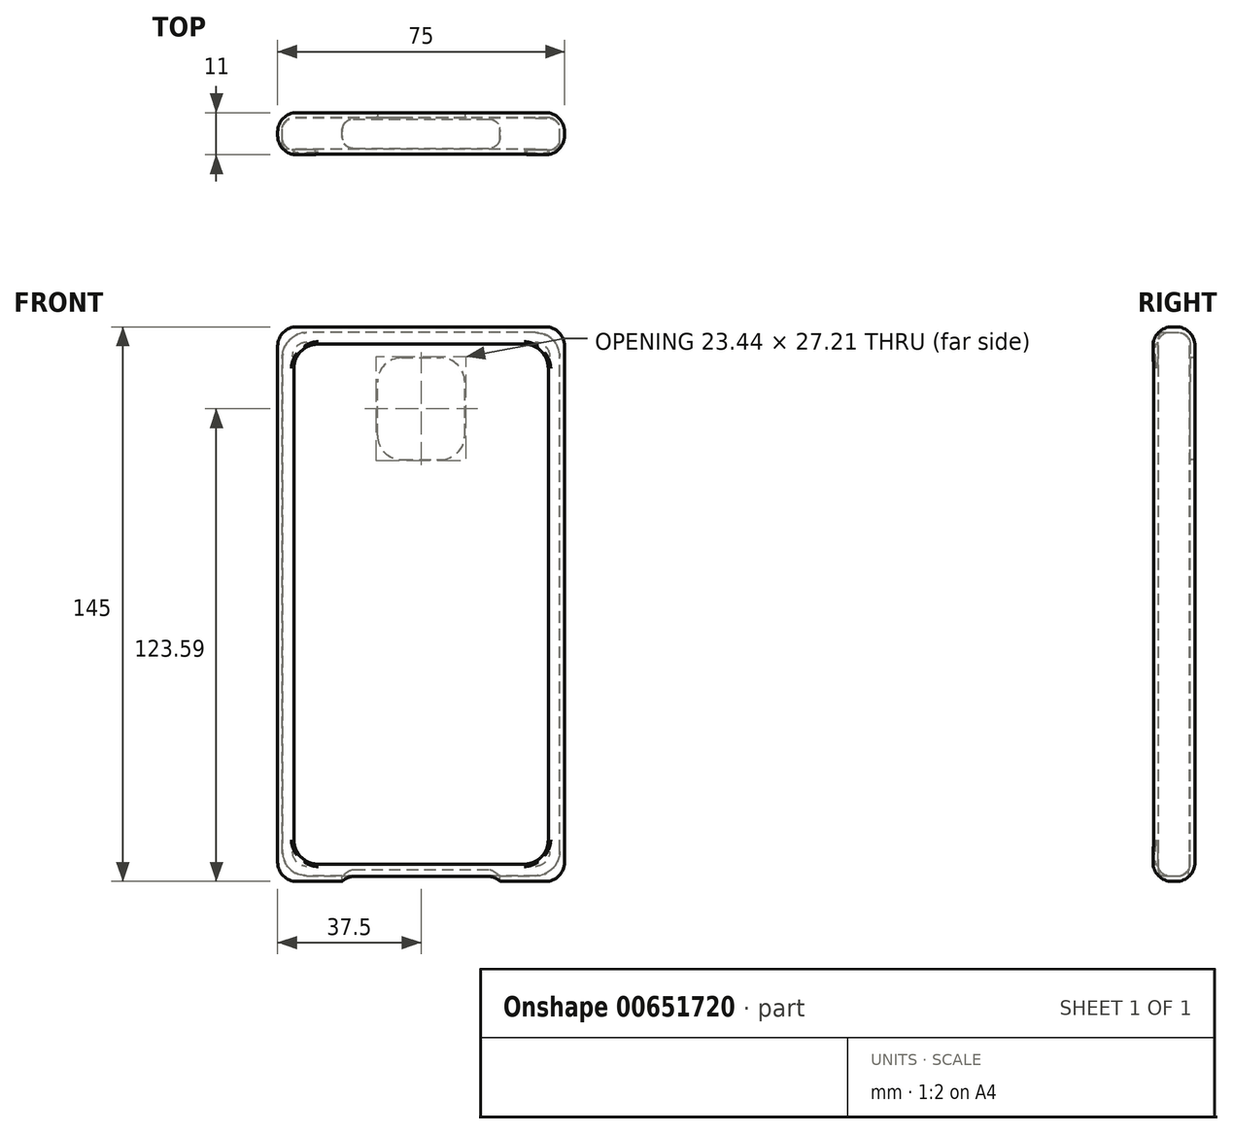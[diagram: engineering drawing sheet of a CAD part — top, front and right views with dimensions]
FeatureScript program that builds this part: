
annotation { "Feature Type Name" : "Feature", "Feature Type Description" : "" }
export const myFeature = defineFeature(function(context is Context, id is Id, definition is map)
    precondition{}
    {
        {
            var Q0;
            Q0=qCreatedBy(makeId("Front.planeOp"),FACE);
            var sketch = newSketch(context, id + "F0", { "sketchPlane" : qUnion([Q0])});
            skLineSegment(sketch, "E0.bottom", {"start": v(29.9, -71) * mm, "end": v(-29.9, -71) * mm});
            skLineSegment(sketch, "E0.top", {"start": v(29.9, 71) * mm, "end": v(-29.9, 71) * mm});
            skLineSegment(sketch, "E0.left", {"start": v(36.25, -64.65) * mm, "end": v(36.25, 64.65) * mm});
            skLineSegment(sketch, "E0.right", {"start": v(-36.25, -64.65) * mm, "end": v(-36.25, 64.65) * mm});
            skPoint(sketch, "E0.middle", {"position": v(0, 0) * mm});
            skPoint(sketch, "E1.visualSharp", {"position": v(-36.25, 71) * mm});
            skArc(sketch, "E1.filletArc", {"start": v(-29.9, 71) * mm, "mid": v(-34.4, 69.14) * mm, "end": v(-36.25, 64.65) * mm});
            skPoint(sketch, "E2.visualSharp", {"position": v(36.25, 71) * mm});
            skArc(sketch, "E2.filletArc", {"start": v(36.25, 64.65) * mm, "mid": v(34.4, 69.14) * mm, "end": v(29.9, 71) * mm});
            skPoint(sketch, "E3.visualSharp", {"position": v(36.25, -71) * mm});
            skArc(sketch, "E3.filletArc", {"start": v(29.9, -71) * mm, "mid": v(34.4, -69.14) * mm, "end": v(36.25, -64.65) * mm});
            skPoint(sketch, "E4.visualSharp", {"position": v(-36.25, -71) * mm});
            skArc(sketch, "E4.filletArc", {"start": v(-36.25, -64.65) * mm, "mid": v(-34.4, -69.14) * mm, "end": v(-29.9, -71) * mm});
            skSolve(sketch);
        }
        {
            var Q0;
            Q0=makeQuery(id+"F0.imprint","IMPRINT",FACE,{"disambiguationData":[TD([[makeQuery(id+"F0.imprint","IMPRINT",EDGE,{"derivedFrom":sQuery(id+"F0.wireOp",EDGE,"E0.bottom")}),-1.0]])]});
            extrude(context, id + "F1", {"entities" : qUnion([Q0]), "endBound" : BoundingType.SYMMETRIC, "depth" : 8.1 * mm, "offsetDistance" : 25.4 * mm});
        }
        {
            var Q0;
            Q0=makeQuery(id+"F1.opExtrude","CAP_FACE",FACE,{"disambiguationData":[OSD([sQuery(id+"F0.wireOp",EDGE,"E0.bottom"),sQuery(id+"F0.wireOp",EDGE,"E0.top"),sQuery(id+"F0.wireOp",EDGE,"E0.left"),sQuery(id+"F0.wireOp",EDGE,"E0.right"),sQuery(id+"F0.wireOp",EDGE,"E1.filletArc"),sQuery(id+"F0.wireOp",EDGE,"E2.filletArc"),sQuery(id+"F0.wireOp",EDGE,"E3.filletArc"),sQuery(id+"F0.wireOp",EDGE,"E4.filletArc")])],"isStart":false});
            fillet(context, id + "F2", {"entities" : qUnion([Q0]), "radius" : 1.27 * mm, "tangentPropagation" : true, "allowEdgeOverflow" : false});
        }
        {
            var Q0;
            Q0=makeQuery(id+"F1.opExtrude","CAP_FACE",FACE,{"disambiguationData":[OSD([sQuery(id+"F0.wireOp",EDGE,"E0.bottom"),sQuery(id+"F0.wireOp",EDGE,"E0.top"),sQuery(id+"F0.wireOp",EDGE,"E0.left"),sQuery(id+"F0.wireOp",EDGE,"E0.right"),sQuery(id+"F0.wireOp",EDGE,"E1.filletArc"),sQuery(id+"F0.wireOp",EDGE,"E2.filletArc"),sQuery(id+"F0.wireOp",EDGE,"E3.filletArc"),sQuery(id+"F0.wireOp",EDGE,"E4.filletArc")])],"isStart":true});
            fillet(context, id + "F3", {"entities" : qUnion([Q0]), "radius" : 2.54 * mm, "rho" : .3, "crossSection" : FilletCrossSection.CONIC, "allowEdgeOverflow" : false});
        }
        {
            var Q0;
            Q0=qCreatedBy(makeId("Front.planeOp"),FACE);
            var sketch = newSketch(context, id + "F4", { "sketchPlane" : qUnion([Q0])});
            skLineSegment(sketch, "E5.bottom", {"start": v(37.5, -72.5) * mm, "end": v(-37.5, -72.5) * mm});
            skLineSegment(sketch, "E5.top", {"start": v(37.5, 72.5) * mm, "end": v(-37.5, 72.5) * mm});
            skLineSegment(sketch, "E5.left", {"start": v(37.5, -72.5) * mm, "end": v(37.5, 72.5) * mm});
            skLineSegment(sketch, "E5.right", {"start": v(-37.5, -72.5) * mm, "end": v(-37.5, 72.5) * mm});
            skPoint(sketch, "E5.middle", {"position": v(0, 0) * mm});
            skSolve(sketch);
        }
        {
            var Q0;
            Q0 = qSketchRegion(id + "F4", true);
            extrude(context, id + "F5", {"entities" : qUnion([Q0]), "endBound" : BoundingType.SYMMETRIC, "depth" : 11 * mm, "offsetDistance" : 25 * mm});
        }
        {
            var Q0;
            Q0=makeQuery(id+"F5.opExtrude","SWEPT_EDGE",EDGE,{"disambiguationData":[OSD([sQuery(id+"F4.wireOp",EDGE,"E5.top"),sQuery(id+"F4.wireOp",EDGE,"E5.right")])]});
            var Q1;
            Q1=makeQuery(id+"F5.opExtrude","SWEPT_EDGE",EDGE,{"disambiguationData":[OSD([sQuery(id+"F4.wireOp",EDGE,"E5.top"),sQuery(id+"F4.wireOp",EDGE,"E5.left")])]});
            var Q2;
            Q2=makeQuery(id+"F5.opExtrude","SWEPT_EDGE",EDGE,{"disambiguationData":[OSD([sQuery(id+"F4.wireOp",EDGE,"E5.bottom"),sQuery(id+"F4.wireOp",EDGE,"E5.right")])]});
            var Q3;
            Q3=makeQuery(id+"F5.opExtrude","SWEPT_EDGE",EDGE,{"disambiguationData":[OSD([sQuery(id+"F4.wireOp",EDGE,"E5.bottom"),sQuery(id+"F4.wireOp",EDGE,"E5.left")])]});
            fillet(context, id + "F6", {"entities" : qUnion([Q0, Q1, Q2, Q3]), "radius" : 5 * mm, "tangentPropagation" : true, "allowEdgeOverflow" : false});
        }
        {
            var Q0;
            Q0=makeQuery(id+"F5.opExtrude","CAP_FACE",FACE,{"disambiguationData":[OSD([sQuery(id+"F4.wireOp",EDGE,"E5.bottom"),sQuery(id+"F4.wireOp",EDGE,"E5.top"),sQuery(id+"F4.wireOp",EDGE,"E5.left"),sQuery(id+"F4.wireOp",EDGE,"E5.right")])],"isStart":false});
            var Q1;
            Q1=makeQuery(id+"F5.opExtrude","CAP_FACE",FACE,{"disambiguationData":[OSD([sQuery(id+"F4.wireOp",EDGE,"E5.bottom"),sQuery(id+"F4.wireOp",EDGE,"E5.top"),sQuery(id+"F4.wireOp",EDGE,"E5.left"),sQuery(id+"F4.wireOp",EDGE,"E5.right")])],"isStart":true});
            fillet(context, id + "F7", {"entities" : qUnion([Q0, Q1]), "radius" : 5 * mm, "tangentPropagation" : true, "allowEdgeOverflow" : false});
        }
        {
            var Q0;
            Q0=qCreatedBy(makeId("Front.planeOp"),FACE);
            var sketch = newSketch(context, id + "F8", { "sketchPlane" : qUnion([Q0])});
            skLineSegment(sketch, "E6.bottom", {"start": v(30.1, -71.2) * mm, "end": v(-30.1, -71.2) * mm});
            skLineSegment(sketch, "E6.top", {"start": v(30.1, 71.2) * mm, "end": v(-30.1, 71.2) * mm});
            skLineSegment(sketch, "E6.left", {"start": v(36.45, -64.85) * mm, "end": v(36.45, 64.85) * mm});
            skLineSegment(sketch, "E6.right", {"start": v(-36.45, -64.85) * mm, "end": v(-36.45, 64.85) * mm});
            skPoint(sketch, "E6.middle", {"position": v(0, 0) * mm});
            skPoint(sketch, "E7.visualSharp", {"position": v(-36.45, 71.2) * mm});
            skArc(sketch, "E7.filletArc", {"start": v(-30.1, 71.2) * mm, "mid": v(-34.6, 69.34) * mm, "end": v(-36.45, 64.85) * mm});
            skPoint(sketch, "E8.visualSharp", {"position": v(36.45, 71.2) * mm});
            skArc(sketch, "E8.filletArc", {"start": v(36.45, 64.85) * mm, "mid": v(34.6, 69.34) * mm, "end": v(30.1, 71.2) * mm});
            skPoint(sketch, "E9.visualSharp", {"position": v(36.45, -71.2) * mm});
            skArc(sketch, "E9.filletArc", {"start": v(30.1, -71.2) * mm, "mid": v(34.6, -69.34) * mm, "end": v(36.45, -64.85) * mm});
            skPoint(sketch, "E10.visualSharp", {"position": v(-36.45, -71.2) * mm});
            skArc(sketch, "E10.filletArc", {"start": v(-36.45, -64.85) * mm, "mid": v(-34.6, -69.34) * mm, "end": v(-30.1, -71.2) * mm});
            skLineSegment(sketch, "E11.bottom", {"start": v(26.9, -68) * mm, "end": v(-26.9, -68) * mm});
            skLineSegment(sketch, "E11.top", {"start": v(26.9, 68) * mm, "end": v(-26.9, 68) * mm});
            skLineSegment(sketch, "E11.left", {"start": v(33.25, -61.65) * mm, "end": v(33.25, 61.65) * mm});
            skLineSegment(sketch, "E11.right", {"start": v(-33.25, -61.65) * mm, "end": v(-33.25, 61.65) * mm});
            skPoint(sketch, "E12.visualSharp", {"position": v(-33.25, 68) * mm});
            skArc(sketch, "E12.filletArc", {"start": v(-26.9, 68) * mm, "mid": v(-31.4, 66.14) * mm, "end": v(-33.25, 61.65) * mm});
            skPoint(sketch, "E13.visualSharp", {"position": v(33.25, 68) * mm});
            skArc(sketch, "E13.filletArc", {"start": v(33.25, 61.65) * mm, "mid": v(31.4, 66.14) * mm, "end": v(26.9, 68) * mm});
            skPoint(sketch, "E14.visualSharp", {"position": v(-33.25, -68) * mm});
            skArc(sketch, "E14.filletArc", {"start": v(-33.25, -61.65) * mm, "mid": v(-31.4, -66.14) * mm, "end": v(-26.9, -68) * mm});
            skPoint(sketch, "E15.visualSharp", {"position": v(33.25, -68) * mm});
            skArc(sketch, "E15.filletArc", {"start": v(26.9, -68) * mm, "mid": v(31.4, -66.14) * mm, "end": v(33.25, -61.65) * mm});
            skSolve(sketch);
        }
        {
            var Q0;
            Q0=makeQuery(id+"F0.imprint","IMPRINT",FACE,{"disambiguationData":[TD([[makeQuery(id+"F0.imprint","IMPRINT",EDGE,{"derivedFrom":sQuery(id+"F0.wireOp",EDGE,"E0.bottom")}),-1.0]])]});
            var Q1;
            Q1=makeQuery(id+"F8.imprint","IMPRINT",FACE,{"disambiguationData":[TD([[makeQuery(id+"F8.imprint","IMPRINT",EDGE,{"derivedFrom":sQuery(id+"F8.wireOp",EDGE,"E11.bottom")}),-1.0]])]});
            extrude(context, id + "F9", {"entities" : qUnion([Q0, Q1]), "endBound" : BoundingType.SYMMETRIC, "depth" : 8.5 * mm, "offsetDistance" : 25 * mm});
        }
        {
            var Q0;
            Q0=makeQuery(id+"F9.opExtrude","SWEPT_BODY",BODY,{"disambiguationData":[OSD([sQuery(id+"F8.wireOp",EDGE,"E11.bottom"),sQuery(id+"F8.wireOp",EDGE,"E11.top"),sQuery(id+"F8.wireOp",EDGE,"E11.left"),sQuery(id+"F8.wireOp",EDGE,"E11.right"),sQuery(id+"F8.wireOp",EDGE,"E12.filletArc"),sQuery(id+"F8.wireOp",EDGE,"E13.filletArc"),sQuery(id+"F8.wireOp",EDGE,"E14.filletArc"),sQuery(id+"F8.wireOp",EDGE,"E15.filletArc")])]});
            transform(context, id + "F10", {"entities" : qUnion([Q0]), "transformType" : TransformType.TRANSLATION_3D, "dx" : 0 * mm, "dy" : -8.5 * mm, "dz" : 0 * mm, "makeCopy" : false});
        }
        {
            var Q0;
            Q0=makeQuery(id+"F9.opExtrude","SWEPT_FACE",FACE,{"disambiguationData":[OSD([sQuery(id+"F0.wireOp",EDGE,"E0.right")])]});
            var Q1;
            Q1=makeQuery(id+"F9.opExtrude","SWEPT_FACE",FACE,{"disambiguationData":[OSD([sQuery(id+"F0.wireOp",EDGE,"E0.bottom")])]});
            var Q2;
            Q2=makeQuery(id+"F9.opExtrude","SWEPT_FACE",FACE,{"disambiguationData":[OSD([sQuery(id+"F0.wireOp",EDGE,"E0.left")])]});
            var Q3;
            Q3=makeQuery(id+"F9.opExtrude","SWEPT_FACE",FACE,{"disambiguationData":[OSD([sQuery(id+"F0.wireOp",EDGE,"E0.top")])]});
            fillet(context, id + "F11", {"entities" : qUnion([Q0, Q1, Q2, Q3]), "radius" : 2.54 * mm, "rho" : .3, "crossSection" : FilletCrossSection.CONIC, "allowEdgeOverflow" : false});
        }
        {
            var Q0;
            Q0=makeQuery(id+"F5.opExtrude","CAP_FACE",FACE,{"disambiguationData":[OSD([sQuery(id+"F4.wireOp",EDGE,"E5.bottom"),sQuery(id+"F4.wireOp",EDGE,"E5.top"),sQuery(id+"F4.wireOp",EDGE,"E5.left"),sQuery(id+"F4.wireOp",EDGE,"E5.right")])],"isStart":true});
            var sketch = newSketch(context, id + "F12", { "sketchPlane" : qUnion([Q0])});
            skLineSegment(sketch, "E16.bottom", {"start": v(5.07, 37.79) * mm, "end": v(-5.07, 37.79) * mm});
            skLineSegment(sketch, "E16.top", {"start": v(5.07, 64.4) * mm, "end": v(-5.07, 64.4) * mm});
            skLineSegment(sketch, "E16.left", {"start": v(11.42, 44.14) * mm, "end": v(11.42, 58.04) * mm});
            skLineSegment(sketch, "E16.right", {"start": v(-11.42, 44.14) * mm, "end": v(-11.42, 58.04) * mm});
            skPoint(sketch, "E16.middle", {"position": v(0, 51.09) * mm});
            skPoint(sketch, "E17.visualSharp", {"position": v(-11.42, 64.4) * mm});
            skArc(sketch, "E17.filletArc", {"start": v(-5.07, 64.4) * mm, "mid": v(-9.56, 62.53) * mm, "end": v(-11.42, 58.04) * mm});
            skPoint(sketch, "E18.visualSharp", {"position": v(11.42, 64.4) * mm});
            skArc(sketch, "E18.filletArc", {"start": v(11.42, 58.04) * mm, "mid": v(9.56, 62.53) * mm, "end": v(5.07, 64.4) * mm});
            skPoint(sketch, "E19.visualSharp", {"position": v(11.42, 37.79) * mm});
            skArc(sketch, "E19.filletArc", {"start": v(5.07, 37.79) * mm, "mid": v(9.56, 39.65) * mm, "end": v(11.42, 44.14) * mm});
            skPoint(sketch, "E20.visualSharp", {"position": v(-11.42, 37.79) * mm});
            skArc(sketch, "E20.filletArc", {"start": v(-11.42, 44.14) * mm, "mid": v(-9.56, 39.65) * mm, "end": v(-5.07, 37.79) * mm});
            skSolve(sketch);
        }
        {
            var Q0;
            Q0=makeQuery(id+"F12.imprint","IMPRINT",FACE,{"disambiguationData":[TD([[makeQuery(id+"F12.imprint","IMPRINT",EDGE,{"derivedFrom":sQuery(id+"F12.wireOp",EDGE,"E16.bottom")}),-1.0]])]});
            extrude(context, id + "F13", {"entities" : qUnion([Q0]), "depth" : 5 * mm, "offsetDistance" : 25 * mm});
        }
        {
            var Q0;
            Q0=makeQuery(id+"F13.opExtrude","SWEPT_BODY",BODY,{"disambiguationData":[OSD([sQuery(id+"F12.wireOp",EDGE,"E16.bottom"),sQuery(id+"F12.wireOp",EDGE,"E16.top"),sQuery(id+"F12.wireOp",EDGE,"E16.left"),sQuery(id+"F12.wireOp",EDGE,"E16.right"),sQuery(id+"F12.wireOp",EDGE,"E17.filletArc"),sQuery(id+"F12.wireOp",EDGE,"E18.filletArc"),sQuery(id+"F12.wireOp",EDGE,"E19.filletArc"),sQuery(id+"F12.wireOp",EDGE,"E20.filletArc")])]});
            transform(context, id + "F14", {"entities" : qUnion([Q0]), "transformType" : TransformType.TRANSLATION_3D, "dx" : 0 * mm, "dy" : -1.5 * mm, "dz" : 0 * mm, "makeCopy" : false});
        }
        {
            var Q0;
            Q0=makeQuery(id+"F9.opExtrude","SWEPT_BODY",BODY,{"disambiguationData":[OSD([sQuery(id+"F0.wireOp",EDGE,"E0.bottom"),sQuery(id+"F0.wireOp",EDGE,"E0.top"),sQuery(id+"F0.wireOp",EDGE,"E0.left"),sQuery(id+"F0.wireOp",EDGE,"E0.right"),sQuery(id+"F0.wireOp",EDGE,"E1.filletArc"),sQuery(id+"F0.wireOp",EDGE,"E2.filletArc"),sQuery(id+"F0.wireOp",EDGE,"E3.filletArc"),sQuery(id+"F0.wireOp",EDGE,"E4.filletArc")])]});
            var Q1;
            Q1=makeQuery(id+"F9.opExtrude","SWEPT_BODY",BODY,{"disambiguationData":[OSD([sQuery(id+"F8.wireOp",EDGE,"E11.bottom"),sQuery(id+"F8.wireOp",EDGE,"E11.top"),sQuery(id+"F8.wireOp",EDGE,"E11.left"),sQuery(id+"F8.wireOp",EDGE,"E11.right"),sQuery(id+"F8.wireOp",EDGE,"E12.filletArc"),sQuery(id+"F8.wireOp",EDGE,"E13.filletArc"),sQuery(id+"F8.wireOp",EDGE,"E14.filletArc"),sQuery(id+"F8.wireOp",EDGE,"E15.filletArc")])]});
            var Q2;
            Q2=makeQuery(id+"F13.opExtrude","SWEPT_BODY",BODY,{"disambiguationData":[OSD([sQuery(id+"F12.wireOp",EDGE,"E16.bottom"),sQuery(id+"F12.wireOp",EDGE,"E16.top"),sQuery(id+"F12.wireOp",EDGE,"E16.left"),sQuery(id+"F12.wireOp",EDGE,"E16.right"),sQuery(id+"F12.wireOp",EDGE,"E17.filletArc"),sQuery(id+"F12.wireOp",EDGE,"E18.filletArc"),sQuery(id+"F12.wireOp",EDGE,"E19.filletArc"),sQuery(id+"F12.wireOp",EDGE,"E20.filletArc")])]});
            var Q3;
            Q3=makeQuery(id+"F5.opExtrude","SWEPT_BODY",BODY,{"disambiguationData":[OSD([sQuery(id+"F4.wireOp",EDGE,"E5.bottom"),sQuery(id+"F4.wireOp",EDGE,"E5.top"),sQuery(id+"F4.wireOp",EDGE,"E5.left"),sQuery(id+"F4.wireOp",EDGE,"E5.right")])]});
            booleanBodies(context, id + "F15", {"operationType" : BooleanOperationType.SUBTRACTION, "tools" : qUnion([Q0, Q1, Q2]), "targets" : qUnion([Q3])});
        }
        {
            var Q0;
            Q0=makeQuery(id+"F15.opBoolean","COPY",FACE,{"derivedFrom":makeQuery(id+"F9.opExtrude","SWEPT_FACE",FACE,{"disambiguationData":[OSD([sQuery(id+"F8.wireOp",EDGE,"E11.top")])]})});
            var Q1;
            Q1=makeQuery(id+"F15.opBoolean","COPY",FACE,{"derivedFrom":makeQuery(id+"F9.opExtrude","SWEPT_FACE",FACE,{"disambiguationData":[OSD([sQuery(id+"F8.wireOp",EDGE,"E13.filletArc")])]})});
            var Q2;
            Q2=makeQuery(id+"F15.opBoolean","COPY",FACE,{"derivedFrom":makeQuery(id+"F9.opExtrude","SWEPT_FACE",FACE,{"disambiguationData":[OSD([sQuery(id+"F8.wireOp",EDGE,"E11.left")])]})});
            var Q3;
            Q3=makeQuery(id+"F15.opBoolean","COPY",FACE,{"derivedFrom":makeQuery(id+"F9.opExtrude","SWEPT_FACE",FACE,{"disambiguationData":[OSD([sQuery(id+"F8.wireOp",EDGE,"E15.filletArc")])]})});
            var Q4;
            Q4=makeQuery(id+"F15.opBoolean","COPY",FACE,{"derivedFrom":makeQuery(id+"F9.opExtrude","SWEPT_FACE",FACE,{"disambiguationData":[OSD([sQuery(id+"F8.wireOp",EDGE,"E11.bottom")])]})});
            var Q5;
            Q5=makeQuery(id+"F15.opBoolean","COPY",FACE,{"derivedFrom":makeQuery(id+"F9.opExtrude","SWEPT_FACE",FACE,{"disambiguationData":[OSD([sQuery(id+"F8.wireOp",EDGE,"E14.filletArc")])]})});
            var Q6;
            Q6=makeQuery(id+"F15.opBoolean","COPY",FACE,{"derivedFrom":makeQuery(id+"F9.opExtrude","SWEPT_FACE",FACE,{"disambiguationData":[OSD([sQuery(id+"F8.wireOp",EDGE,"E11.right")])]})});
            var Q7;
            Q7=makeQuery(id+"F15.opBoolean","COPY",FACE,{"derivedFrom":makeQuery(id+"F9.opExtrude","SWEPT_FACE",FACE,{"disambiguationData":[OSD([sQuery(id+"F8.wireOp",EDGE,"E12.filletArc")])]})});
            fillet(context, id + "F16", {"entities" : qUnion([Q0, Q1, Q2, Q3, Q4, Q5, Q6, Q7]), "radius" : .5 * mm, "allowEdgeOverflow" : false});
        }
        {
            var Q0;
            Q0=makeQuery(id+"F15.opBoolean","COPY",FACE,{"derivedFrom":makeQuery(id+"F13.opExtrude","SWEPT_FACE",FACE,{"disambiguationData":[OSD([sQuery(id+"F12.wireOp",EDGE,"E18.filletArc")])]})});
            var Q1;
            Q1=makeQuery(id+"F15.opBoolean","COPY",FACE,{"derivedFrom":makeQuery(id+"F13.opExtrude","SWEPT_FACE",FACE,{"disambiguationData":[OSD([sQuery(id+"F12.wireOp",EDGE,"E16.left")])]})});
            var Q2;
            Q2=makeQuery(id+"F15.opBoolean","COPY",FACE,{"derivedFrom":makeQuery(id+"F13.opExtrude","SWEPT_FACE",FACE,{"disambiguationData":[OSD([sQuery(id+"F12.wireOp",EDGE,"E19.filletArc")])]})});
            var Q3;
            Q3=makeQuery(id+"F15.opBoolean","COPY",FACE,{"derivedFrom":makeQuery(id+"F13.opExtrude","SWEPT_FACE",FACE,{"disambiguationData":[OSD([sQuery(id+"F12.wireOp",EDGE,"E16.bottom")])]})});
            var Q4;
            Q4=makeQuery(id+"F15.opBoolean","COPY",FACE,{"derivedFrom":makeQuery(id+"F13.opExtrude","SWEPT_FACE",FACE,{"disambiguationData":[OSD([sQuery(id+"F12.wireOp",EDGE,"E20.filletArc")])]})});
            var Q5;
            Q5=makeQuery(id+"F15.opBoolean","COPY",FACE,{"derivedFrom":makeQuery(id+"F13.opExtrude","SWEPT_FACE",FACE,{"disambiguationData":[OSD([sQuery(id+"F12.wireOp",EDGE,"E16.right")])]})});
            var Q6;
            Q6=makeQuery(id+"F15.opBoolean","COPY",FACE,{"derivedFrom":makeQuery(id+"F13.opExtrude","SWEPT_FACE",FACE,{"disambiguationData":[OSD([sQuery(id+"F12.wireOp",EDGE,"E17.filletArc")])]})});
            var Q7;
            Q7=makeQuery(id+"F15.opBoolean","COPY",FACE,{"derivedFrom":makeQuery(id+"F13.opExtrude","SWEPT_FACE",FACE,{"disambiguationData":[OSD([sQuery(id+"F12.wireOp",EDGE,"E16.top")])]})});
            fillet(context, id + "F17", {"entities" : qUnion([Q0, Q1, Q2, Q3, Q4, Q5, Q6, Q7]), "radius" : .3 * mm, "allowEdgeOverflow" : false});
        }
        {
            var Q0;
            Q0=qCreatedBy(makeId("Top.planeOp"),FACE);
            var sketch = newSketch(context, id + "F18", { "sketchPlane" : qUnion([Q0])});
            skLineSegment(sketch, "E21.bottom", {"start": v(17.64, 3.87) * mm, "end": v(-17.64, 3.87) * mm});
            skLineSegment(sketch, "E21.top", {"start": v(17.64, -3.87) * mm, "end": v(-17.64, -3.87) * mm});
            skLineSegment(sketch, "E21.left", {"start": v(20.64, 0.87) * mm, "end": v(20.64, -0.87) * mm});
            skLineSegment(sketch, "E21.right", {"start": v(-20.64, 0.87) * mm, "end": v(-20.64, -0.87) * mm});
            skPoint(sketch, "E21.middle", {"position": v(0, 0) * mm});
            skPoint(sketch, "E22.visualSharp", {"position": v(-20.64, -3.87) * mm});
            skArc(sketch, "E22.filletArc", {"start": v(-20.64, -0.87) * mm, "mid": v(-19.76, -3) * mm, "end": v(-17.64, -3.87) * mm});
            skPoint(sketch, "E23.visualSharp", {"position": v(-20.64, 3.87) * mm});
            skArc(sketch, "E23.filletArc", {"start": v(-17.64, 3.87) * mm, "mid": v(-19.76, 3) * mm, "end": v(-20.64, 0.87) * mm});
            skPoint(sketch, "E24.visualSharp", {"position": v(20.64, 3.87) * mm});
            skArc(sketch, "E24.filletArc", {"start": v(20.64, 0.87) * mm, "mid": v(19.76, 3) * mm, "end": v(17.64, 3.87) * mm});
            skPoint(sketch, "E25.visualSharp", {"position": v(20.64, -3.87) * mm});
            skArc(sketch, "E25.filletArc", {"start": v(17.64, -3.87) * mm, "mid": v(19.76, -3) * mm, "end": v(20.64, -0.87) * mm});
            skSolve(sketch);
        }
        {
            var Q0;
            Q0=makeQuery(id+"F18.imprint","IMPRINT",FACE,{"disambiguationData":[TD([[makeQuery(id+"F18.imprint","IMPRINT",EDGE,{"derivedFrom":sQuery(id+"F18.wireOp",EDGE,"E21.bottom")}),1.0]])]});
            extrude(context, id + "F19", {"entities" : qUnion([Q0]), "oppositeDirection" : true, "depth" : 5 * mm, "offsetDistance" : 25 * mm});
        }
        {
            var Q0;
            Q0=makeQuery(id+"F19.opExtrude","SWEPT_BODY",BODY,{"disambiguationData":[OSD([sQuery(id+"F18.wireOp",EDGE,"E21.bottom"),sQuery(id+"F18.wireOp",EDGE,"E21.top"),sQuery(id+"F18.wireOp",EDGE,"E21.left"),sQuery(id+"F18.wireOp",EDGE,"E21.right"),sQuery(id+"F18.wireOp",EDGE,"E22.filletArc"),sQuery(id+"F18.wireOp",EDGE,"E23.filletArc"),sQuery(id+"F18.wireOp",EDGE,"E24.filletArc"),sQuery(id+"F18.wireOp",EDGE,"E25.filletArc")])]});
            transform(context, id + "F20", {"entities" : qUnion([Q0]), "transformType" : TransformType.TRANSLATION_3D, "dx" : 0 * mm, "dy" : 0 * mm, "dz" : -68.5 * mm, "makeCopy" : false});
        }
        {
            var Q0;
            Q0=makeQuery(id+"F19.opExtrude","SWEPT_BODY",BODY,{"disambiguationData":[OSD([sQuery(id+"F18.wireOp",EDGE,"E21.bottom"),sQuery(id+"F18.wireOp",EDGE,"E21.top"),sQuery(id+"F18.wireOp",EDGE,"E21.left"),sQuery(id+"F18.wireOp",EDGE,"E21.right"),sQuery(id+"F18.wireOp",EDGE,"E22.filletArc"),sQuery(id+"F18.wireOp",EDGE,"E23.filletArc"),sQuery(id+"F18.wireOp",EDGE,"E24.filletArc"),sQuery(id+"F18.wireOp",EDGE,"E25.filletArc")])]});
            var Q1;
            Q1=makeQuery(id+"F5.opExtrude","SWEPT_BODY",BODY,{"disambiguationData":[OSD([sQuery(id+"F4.wireOp",EDGE,"E5.bottom"),sQuery(id+"F4.wireOp",EDGE,"E5.top"),sQuery(id+"F4.wireOp",EDGE,"E5.left"),sQuery(id+"F4.wireOp",EDGE,"E5.right")])]});
            booleanBodies(context, id + "F21", {"operationType" : BooleanOperationType.SUBTRACTION, "tools" : qUnion([Q0]), "targets" : qUnion([Q1])});
        }
    });
